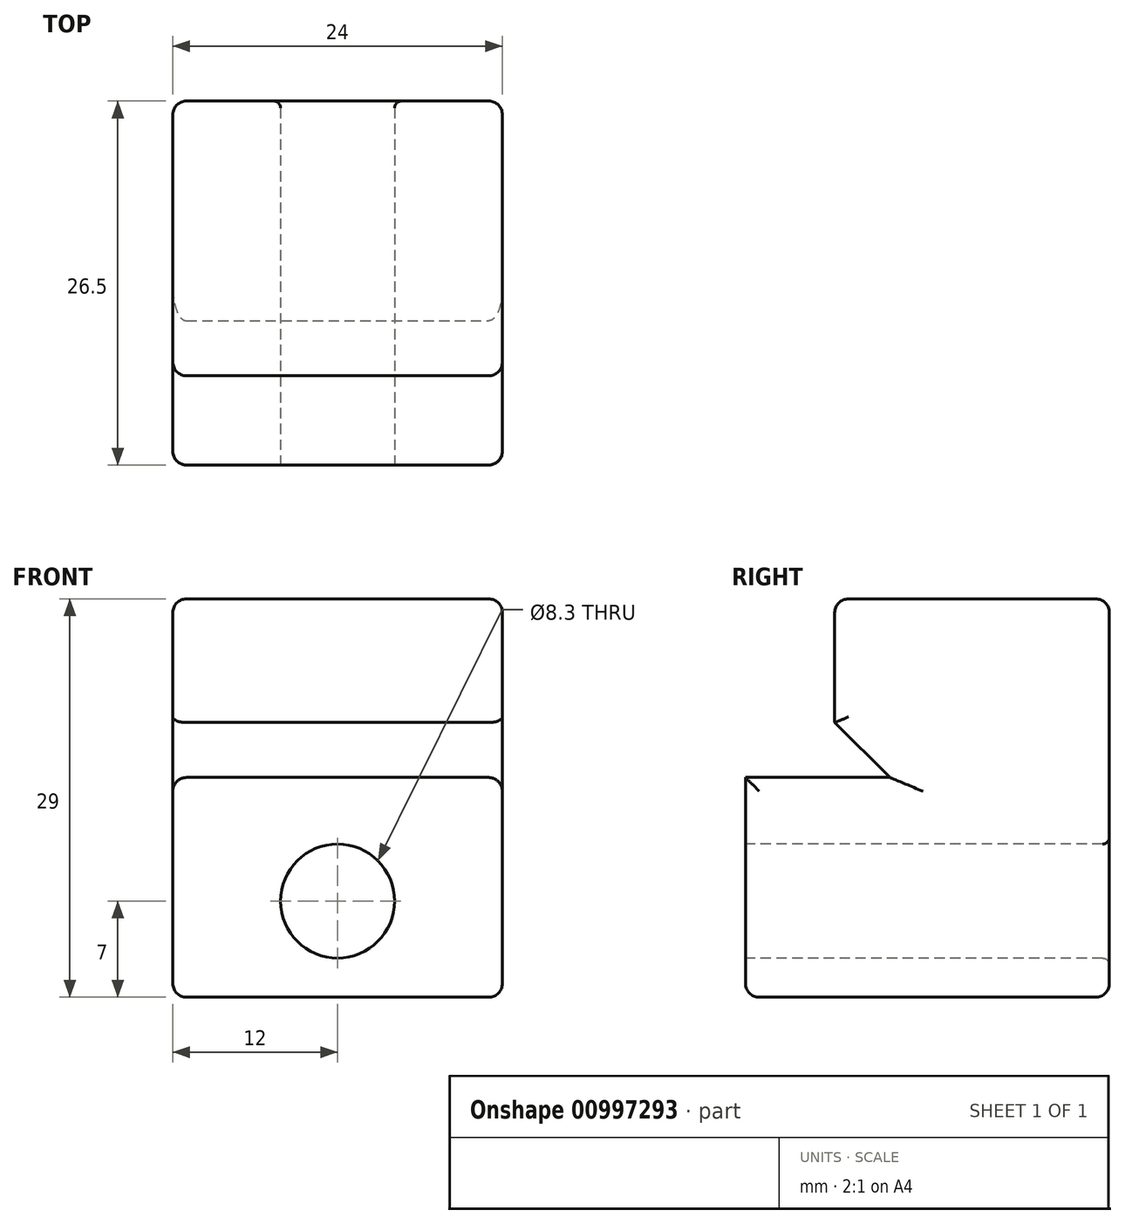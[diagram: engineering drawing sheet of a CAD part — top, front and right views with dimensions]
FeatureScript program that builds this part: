
annotation { "Feature Type Name" : "Feature", "Feature Type Description" : "" }
export const myFeature = defineFeature(function(context is Context, id is Id, definition is map)
    precondition{}
    {
        {
            var Q0;
            Q0=qCreatedBy(makeId("Top.planeOp"),FACE);
            var sketch = newSketch(context, id + "F0", { "sketchPlane" : qUnion([Q0])});
            skLineSegment(sketch, "E0.bottom", {"start": v(12, 13.25) * mm, "end": v(-12, 13.25) * mm});
            skLineSegment(sketch, "E0.top", {"start": v(12, -13.25) * mm, "end": v(-12, -13.25) * mm});
            skLineSegment(sketch, "E0.left", {"start": v(12, 13.25) * mm, "end": v(12, -13.25) * mm});
            skLineSegment(sketch, "E0.right", {"start": v(-12, 13.25) * mm, "end": v(-12, -13.25) * mm});
            skPoint(sketch, "E0.middle", {"position": v(0, 0) * mm});
            skSolve(sketch);
        }
        {
            var Q0;
            Q0 = qSketchRegion(id + "F0", true);
            extrude(context, id + "F1", {"entities" : qUnion([Q0]), "depth" : 29 * mm, "offsetDistance" : 25 * mm});
        }
        {
            var Q0;
            Q0=makeQuery(id+"F1.opExtrude","SWEPT_FACE",FACE,{"disambiguationData":[OSD([sQuery(id+"F0.wireOp",EDGE,"E0.left")])]});
            var sketch = newSketch(context, id + "F2", { "sketchPlane" : qUnion([Q0])});
            skLineSegment(sketch, "E1", {"start": v(13.25, 29) * mm, "end": v(-6.75, 29) * mm, "construction": true});
            skLineSegment(sketch, "E2", {"start": v(-6.75, 29) * mm, "end": v(-6.75, 20) * mm});
            skLineSegment(sketch, "E3", {"start": v(-13.25, 0) * mm, "end": v(-13.25, 16) * mm, "construction": true});
            skLineSegment(sketch, "E4", {"start": v(-13.25, 16) * mm, "end": v(-2.75, 16) * mm});
            skLineSegment(sketch, "E5", {"start": v(-2.75, 16) * mm, "end": v(-6.75, 20) * mm});
            skSolve(sketch);
        }
        {
            var Q0;
            {var subQ5=sQuery(id+"F2.wireOp",EDGE,"E2");Q0=makeQuery(id+"F2.imprint","IMPRINT",FACE,{"disambiguationData":[TD([[makeQuery(id+"F2.imprint","IMPRINT",EDGE,{"derivedFrom":subQ5}),-1.0]])]});}
            extrude(context, id + "F3", {"entities" : qUnion([Q0]), "operationType" : NewBodyOperationType.REMOVE, "oppositeDirection" : true, "depth" : 25 * mm, "offsetDistance" : 25 * mm});
        }
        {
            var Q0;
            Q0=makeQuery(id+"F1.opExtrude","SWEPT_FACE",FACE,{"disambiguationData":[OSD([sQuery(id+"F0.wireOp",EDGE,"E0.top")])]});
            var sketch = newSketch(context, id + "F4", { "sketchPlane" : qUnion([Q0])});
            skLineSegment(sketch, "E6", {"start": v(0, 0) * mm, "end": v(0, 14) * mm, "construction": true});
            skPoint(sketch, "E6.endSnap0", {"position": v(0, 16) * mm});
            skCircle(sketch, "E7", {"center": v(0, 7) * mm, "radius": 4.15 * mm});
            skSolve(sketch);
        }
        {
            var Q0;
            Q0 = qSketchRegion(id + "F4", true);
            extrude(context, id + "F5", {"entities" : qUnion([Q0]), "operationType" : NewBodyOperationType.REMOVE, "oppositeDirection" : true, "depth" : 31 * mm, "offsetDistance" : 25 * mm});
        }
        {
            var Q0;
            Q0=makeQuery(id+"F1.opExtrude","SWEPT_FACE",FACE,{"disambiguationData":[OSD([sQuery(id+"F0.wireOp",EDGE,"E0.left")])]});
            var Q1;
            Q1=makeQuery(id+"F1.opExtrude","SWEPT_FACE",FACE,{"disambiguationData":[OSD([sQuery(id+"F0.wireOp",EDGE,"E0.right")])]});
            var Q2;
            Q2=makeQuery(id+"F1.opExtrude","CAP_FACE",FACE,{"disambiguationData":[OSD([sQuery(id+"F0.wireOp",EDGE,"E0.bottom"),sQuery(id+"F0.wireOp",EDGE,"E0.top"),sQuery(id+"F0.wireOp",EDGE,"E0.left"),sQuery(id+"F0.wireOp",EDGE,"E0.right")])],"isStart":false});
            var Q3;
            Q3=makeQuery(id+"F1.opExtrude","CAP_FACE",FACE,{"disambiguationData":[OSD([sQuery(id+"F0.wireOp",EDGE,"E0.bottom"),sQuery(id+"F0.wireOp",EDGE,"E0.top"),sQuery(id+"F0.wireOp",EDGE,"E0.left"),sQuery(id+"F0.wireOp",EDGE,"E0.right")])],"isStart":true});
            var Q4;
            Q4=makeQuery(id+"F3.boolean.opBoolean","COPY",EDGE,{"derivedFrom":makeQuery(id+"F3.opExtrude","SWEPT_EDGE",EDGE,{"disambiguationData":[OSD([sQuery(id+"F0.wireOp",EDGE,"E0.top"),sQuery(id+"F0.wireOp",EDGE,"E0.left"),sQuery(id+"F2.wireOp",EDGE,"E4")])]})});
            fillet(context, id + "F6", {"entities" : qUnion([Q0, Q1, Q2, Q3, Q4]), "radius" : 1 * mm, "tangentPropagation" : true, "allowEdgeOverflow" : false});
        }
        {
            var Q0;
            Q0=makeQuery(id+"F5.boolean.opBoolean","INTERSECT",EDGE,{"derivedFrom":[makeQuery(id+"F1.opExtrude","SWEPT_FACE",FACE,{"disambiguationData":[OSD([sQuery(id+"F0.wireOp",EDGE,"E0.bottom")])]}),makeQuery(id+"F5.opExtrude","SWEPT_FACE",FACE,{"disambiguationData":[OSD([sQuery(id+"F4.wireOp",EDGE,"E7")])]})]});
            var Q1;
            Q1=makeQuery(id+"F5.boolean.opBoolean","COPY",EDGE,{"derivedFrom":makeQuery(id+"F5.opExtrude","CAP_EDGE",EDGE,{"disambiguationData":[OSD([sQuery(id+"F4.wireOp",EDGE,"E7")])],"isStart":true})});
            fillet(context, id + "F7", {"entities" : qUnion([Q0, Q1]), "radius" : .5 * mm, "tangentPropagation" : true, "allowEdgeOverflow" : false});
        }
    });
